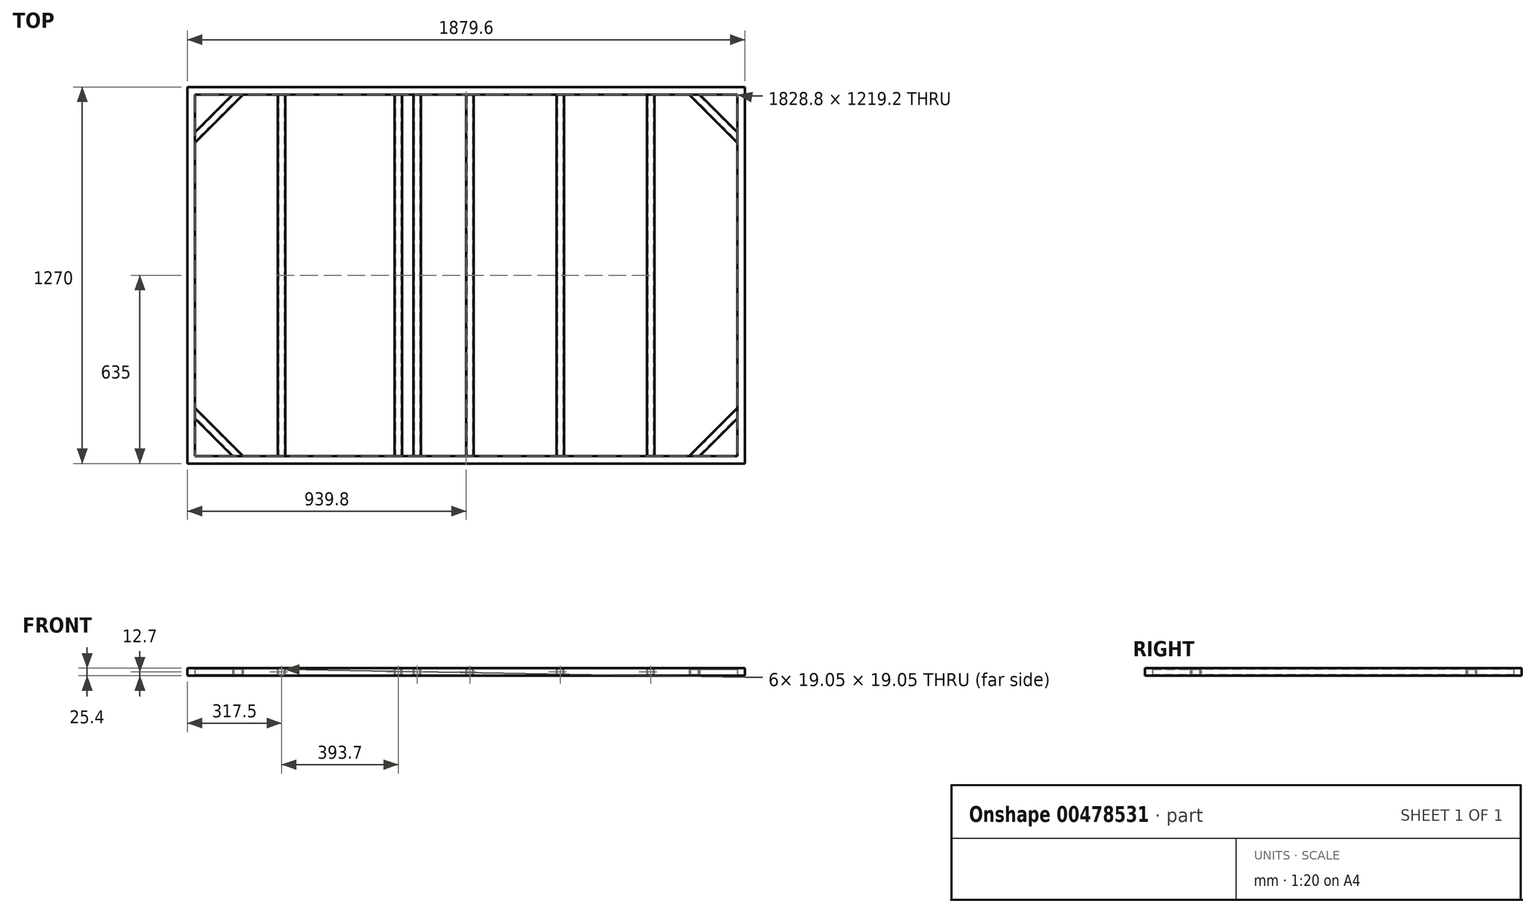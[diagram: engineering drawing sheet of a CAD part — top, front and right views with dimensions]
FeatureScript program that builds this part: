
annotation { "Feature Type Name" : "Feature", "Feature Type Description" : "" }
export const myFeature = defineFeature(function(context is Context, id is Id, definition is map)
    precondition{}
    {
        {
            var Q0;
            Q0=qCreatedBy(makeId("Top.planeOp"),FACE);
            var sketch = newSketch(context, id + "F0", { "sketchPlane" : qUnion([Q0])});
            skLineSegment(sketch, "E0.bottom", {"start": v(0, 0) * mm, "end": v(-1828.8, 0) * mm});
            skLineSegment(sketch, "E0.top", {"start": v(0, 1219.2) * mm, "end": v(-1828.8, 1219.2) * mm});
            skLineSegment(sketch, "E0.left", {"start": v(0, 0) * mm, "end": v(0, 1219.2) * mm});
            skLineSegment(sketch, "E0.right", {"start": v(-1828.8, 0) * mm, "end": v(-1828.8, 1219.2) * mm});
            skLineSegment(sketch, "E1.0", {"start": v(25.4, 1244.6) * mm, "end": v(-1854.2, 1244.6) * mm});
            skLineSegment(sketch, "E1.1", {"start": v(25.4, -25.4) * mm, "end": v(25.4, 1244.6) * mm});
            skLineSegment(sketch, "E1.2", {"start": v(25.4, -25.4) * mm, "end": v(-1854.2, -25.4) * mm});
            skLineSegment(sketch, "E1.3", {"start": v(-1854.2, -25.4) * mm, "end": v(-1854.2, 1244.6) * mm});
            skSolve(sketch);
        }
        {
            var Q0;
            Q0=makeQuery(id+"F0.imprint","IMPRINT",FACE,{"disambiguationData":[TD([[makeQuery(id+"F0.imprint","IMPRINT",EDGE,{"derivedFrom":sQuery(id+"F0.wireOp",EDGE,"E0.bottom")}),1.0]])]});
            extrude(context, id + "F1", {"entities" : qUnion([Q0]), "depth" : 25.4 * mm});
        }
        {
            var Q0;
            Q0=makeQuery(id+"F1.opExtrude","CAP_FACE",FACE,{"disambiguationData":[OSD([sQuery(id+"F0.wireOp",EDGE,"E0.bottom"),sQuery(id+"F0.wireOp",EDGE,"E0.top"),sQuery(id+"F0.wireOp",EDGE,"E0.left"),sQuery(id+"F0.wireOp",EDGE,"E0.right"),sQuery(id+"F0.wireOp",EDGE,"E1.0"),sQuery(id+"F0.wireOp",EDGE,"E1.1"),sQuery(id+"F0.wireOp",EDGE,"E1.2"),sQuery(id+"F0.wireOp",EDGE,"E1.3")])],"isStart":false});
            var sketch = newSketch(context, id + "F2", { "sketchPlane" : qUnion([Q0])});
            skLineSegment(sketch, "E2.bottom", {"start": v(-1549.4, 1219.2) * mm, "end": v(-1524, 1219.2) * mm});
            skLineSegment(sketch, "E2.top", {"start": v(-1549.4, 0) * mm, "end": v(-1524, 0) * mm});
            skLineSegment(sketch, "E2.left", {"start": v(-1549.4, 1219.2) * mm, "end": v(-1549.4, 0) * mm});
            skLineSegment(sketch, "E2.right", {"start": v(-1524, 1219.2) * mm, "end": v(-1524, 0) * mm});
            skLineSegment(sketch, "E3.bottom", {"start": v(-1092.2, 1219.2) * mm, "end": v(-1066.8, 1219.2) * mm});
            skLineSegment(sketch, "E3.top", {"start": v(-1092.2, 0) * mm, "end": v(-1066.8, 0) * mm});
            skLineSegment(sketch, "E3.left", {"start": v(-1092.2, 1219.2) * mm, "end": v(-1092.2, 0) * mm});
            skLineSegment(sketch, "E3.right", {"start": v(-1066.8, 1219.2) * mm, "end": v(-1066.8, 0) * mm});
            skLineSegment(sketch, "E4.bottom", {"start": v(-1155.7, 1219.2) * mm, "end": v(-1130.3, 1219.2) * mm});
            skLineSegment(sketch, "E4.top", {"start": v(-1155.7, 0) * mm, "end": v(-1130.3, 0) * mm});
            skLineSegment(sketch, "E4.left", {"start": v(-1130.3, 1219.2) * mm, "end": v(-1130.3, 0) * mm});
            skLineSegment(sketch, "E4.right", {"start": v(-1155.7, 1219.2) * mm, "end": v(-1155.7, 0) * mm});
            skLineSegment(sketch, "E5.bottom", {"start": v(-914.4, 1219.2) * mm, "end": v(-889, 1219.2) * mm});
            skLineSegment(sketch, "E5.top", {"start": v(-914.4, 0) * mm, "end": v(-889, 0) * mm});
            skLineSegment(sketch, "E5.left", {"start": v(-914.4, 1219.2) * mm, "end": v(-914.4, 0) * mm});
            skLineSegment(sketch, "E5.right", {"start": v(-889, 1219.2) * mm, "end": v(-889, 0) * mm});
            skLineSegment(sketch, "E6.bottom", {"start": v(-609.6, 1219.2) * mm, "end": v(-584.2, 1219.2) * mm});
            skLineSegment(sketch, "E6.top", {"start": v(-609.6, 0) * mm, "end": v(-584.2, 0) * mm});
            skLineSegment(sketch, "E6.left", {"start": v(-609.6, 1219.2) * mm, "end": v(-609.6, 0) * mm});
            skLineSegment(sketch, "E6.right", {"start": v(-584.2, 1219.2) * mm, "end": v(-584.2, 0) * mm});
            skLineSegment(sketch, "E7.bottom", {"start": v(-304.8, 1219.2) * mm, "end": v(-279.4, 1219.2) * mm});
            skLineSegment(sketch, "E7.top", {"start": v(-304.8, 0) * mm, "end": v(-279.4, 0) * mm});
            skLineSegment(sketch, "E7.left", {"start": v(-304.8, 1219.2) * mm, "end": v(-304.8, 0) * mm});
            skLineSegment(sketch, "E7.right", {"start": v(-279.4, 1219.2) * mm, "end": v(-279.4, 0) * mm});
            skSolve(sketch);
        }
        {
            var Q0;
            Q0=makeQuery(id+"F2.imprint","IMPRINT",FACE,{"disambiguationData":[TD([[makeQuery(id+"F2.imprint","IMPRINT",EDGE,{"derivedFrom":sQuery(id+"F2.wireOp",EDGE,"E2.bottom")}),1.0]])]});
            var Q1;
            Q1=makeQuery(id+"F2.imprint","IMPRINT",FACE,{"disambiguationData":[TD([[makeQuery(id+"F2.imprint","IMPRINT",EDGE,{"derivedFrom":sQuery(id+"F2.wireOp",EDGE,"E4.bottom")}),1.0]])]});
            var Q2;
            Q2=makeQuery(id+"F2.imprint","IMPRINT",FACE,{"disambiguationData":[TD([[makeQuery(id+"F2.imprint","IMPRINT",EDGE,{"derivedFrom":sQuery(id+"F2.wireOp",EDGE,"E3.bottom")}),1.0]])]});
            var Q3;
            Q3=makeQuery(id+"F2.imprint","IMPRINT",FACE,{"disambiguationData":[TD([[makeQuery(id+"F2.imprint","IMPRINT",EDGE,{"derivedFrom":sQuery(id+"F2.wireOp",EDGE,"E5.bottom")}),1.0]])]});
            var Q4;
            Q4=makeQuery(id+"F2.imprint","IMPRINT",FACE,{"disambiguationData":[TD([[makeQuery(id+"F2.imprint","IMPRINT",EDGE,{"derivedFrom":sQuery(id+"F2.wireOp",EDGE,"E6.bottom")}),1.0]])]});
            var Q5;
            Q5=makeQuery(id+"F2.imprint","IMPRINT",FACE,{"disambiguationData":[TD([[makeQuery(id+"F2.imprint","IMPRINT",EDGE,{"derivedFrom":sQuery(id+"F2.wireOp",EDGE,"E7.bottom")}),1.0]])]});
            extrude(context, id + "F3", {"entities" : qUnion([Q0, Q1, Q2, Q3, Q4, Q5]), "oppositeDirection" : true, "depth" : 25.4 * mm});
        }
        {
            var Q0;
            Q0=makeQuery(id+"F1.opExtrude","CAP_FACE",FACE,{"disambiguationData":[OSD([sQuery(id+"F0.wireOp",EDGE,"E0.bottom"),sQuery(id+"F0.wireOp",EDGE,"E0.top"),sQuery(id+"F0.wireOp",EDGE,"E0.left"),sQuery(id+"F0.wireOp",EDGE,"E0.right"),sQuery(id+"F0.wireOp",EDGE,"E1.0"),sQuery(id+"F0.wireOp",EDGE,"E1.1"),sQuery(id+"F0.wireOp",EDGE,"E1.2"),sQuery(id+"F0.wireOp",EDGE,"E1.3")])],"isStart":true});
            var sketch = newSketch(context, id + "F4", { "sketchPlane" : qUnion([Q0])});
            skLineSegment(sketch, "E8", {"start": v(-1701.8, 0) * mm, "end": v(-1828.8, -127) * mm});
            skLineSegment(sketch, "E9", {"start": v(-1665.88, 0) * mm, "end": v(-1828.8, -162.92) * mm});
            skLineSegment(sketch, "E10", {"start": v(-1828.8, -609.6) * mm, "end": v(-1335.47, -609.6) * mm, "construction": true});
            skLineSegment(sketch, "E11", {"start": v(-914.4, 25.4) * mm, "end": v(-914.4, -265.03) * mm, "construction": true});
            skPoint(sketch, "E11.endSnap0", {"position": v(-914.4, 0) * mm});
            skLineSegment(sketch, "E12.MirrorCS", {"start": v(-1701.8, -1219.2) * mm, "end": v(-1828.8, -1092.2) * mm});
            skLineSegment(sketch, "E13.MirrorCS", {"start": v(-1665.88, -1219.2) * mm, "end": v(-1828.8, -1056.28) * mm});
            skLineSegment(sketch, "E14.MirrorCS", {"start": v(-162.92, -1219.2) * mm, "end": v(0, -1056.28) * mm});
            skLineSegment(sketch, "E15.MirrorCS", {"start": v(-127, -1219.2) * mm, "end": v(0, -1092.2) * mm});
            skLineSegment(sketch, "E16.MirrorCS", {"start": v(-127, 0) * mm, "end": v(0, -127) * mm});
            skLineSegment(sketch, "E17.MirrorCS", {"start": v(-162.92, 0) * mm, "end": v(0, -162.92) * mm});
            skSolve(sketch);
        }
        {
            var Q0;
            {var subQ0=sQuery(id+"F4.wireOp",EDGE,"E8");Q0=makeQuery(id+"F4.imprint","IMPRINT",FACE,{"disambiguationData":[TD([[makeQuery(id+"F4.imprint","IMPRINT",EDGE,{"derivedFrom":subQ0}),1.0]])]});}
            var Q1;
            {var subQ0=sQuery(id+"F4.wireOp",EDGE,"E13.MirrorCS");Q1=makeQuery(id+"F4.imprint","IMPRINT",FACE,{"disambiguationData":[TD([[makeQuery(id+"F4.imprint","IMPRINT",EDGE,{"derivedFrom":subQ0}),1.0]])]});}
            var Q2;
            {var subQ0=sQuery(id+"F4.wireOp",EDGE,"E14.MirrorCS");Q2=makeQuery(id+"F4.imprint","IMPRINT",FACE,{"disambiguationData":[TD([[makeQuery(id+"F4.imprint","IMPRINT",EDGE,{"derivedFrom":subQ0}),-1.0]])]});}
            var Q3;
            {var subQ0=sQuery(id+"F4.wireOp",EDGE,"E16.MirrorCS");Q3=makeQuery(id+"F4.imprint","IMPRINT",FACE,{"disambiguationData":[TD([[makeQuery(id+"F4.imprint","IMPRINT",EDGE,{"derivedFrom":subQ0}),-1.0]])]});}
            extrude(context, id + "F5", {"entities" : qUnion([Q0, Q1, Q2, Q3]), "oppositeDirection" : true, "depth" : 25.4 * mm});
        }
        {
            var Q0;
            {var subQ0=sQuery(id+"F0.wireOp",EDGE,"E0.right");var subQ1=makeQuery(id+"F1.opExtrude","CAP_EDGE",EDGE,{"disambiguationData":[OSD([subQ0])],"isStart":true});Q0=makeQuery(id+"F5.opExtrude","SWEPT_FACE",FACE,{"disambiguationData":[OSD([subQ0]),TDD([makeQuery(id+"F4.imprint","IMPRINT",EDGE,{"disambiguationData":[TD([[makeQuery(id+"F4.imprint","INTERSECT",VERTEX,{"derivedFrom":[subQ1,sQuery(id+"F4.wireOp",EDGE,"E13.MirrorCS")]}),-1.0]])],"derivedFrom":subQ1})])]});}
            var Q1;
            {var subQ0=sQuery(id+"F0.wireOp",EDGE,"E0.top");var subQ1=makeQuery(id+"F1.opExtrude","CAP_EDGE",EDGE,{"disambiguationData":[OSD([subQ0])],"isStart":true});Q1=makeQuery(id+"F5.opExtrude","SWEPT_FACE",FACE,{"disambiguationData":[OSD([subQ0]),TDD([makeQuery(id+"F4.imprint","IMPRINT",EDGE,{"disambiguationData":[TD([[makeQuery(id+"F4.imprint","INTERSECT",VERTEX,{"derivedFrom":[subQ1,sQuery(id+"F4.wireOp",EDGE,"E13.MirrorCS")]}),-1.0]])],"derivedFrom":subQ1})])]});}
            shell(context, id + "F6", {"entities" : qUnion([Q0, Q1]), "thickness" : 3.17 * mm});
        }
        {
            var Q0;
            {var subQ0=sQuery(id+"F0.wireOp",EDGE,"E0.right");var subQ1=makeQuery(id+"F1.opExtrude","CAP_EDGE",EDGE,{"disambiguationData":[OSD([subQ0])],"isStart":true});Q0=makeQuery(id+"F5.opExtrude","SWEPT_FACE",FACE,{"disambiguationData":[OSD([subQ0]),TDD([makeQuery(id+"F4.imprint","IMPRINT",EDGE,{"disambiguationData":[TD([[makeQuery(id+"F4.imprint","INTERSECT",VERTEX,{"derivedFrom":[subQ1,sQuery(id+"F4.wireOp",EDGE,"E8")]}),-1.0]])],"derivedFrom":subQ1})])]});}
            var Q1;
            {var subQ0=sQuery(id+"F0.wireOp",EDGE,"E0.bottom");var subQ1=makeQuery(id+"F1.opExtrude","CAP_EDGE",EDGE,{"disambiguationData":[OSD([subQ0])],"isStart":true});Q1=makeQuery(id+"F5.opExtrude","SWEPT_FACE",FACE,{"disambiguationData":[OSD([subQ0]),TDD([makeQuery(id+"F4.imprint","IMPRINT",EDGE,{"disambiguationData":[TD([[makeQuery(id+"F4.imprint","INTERSECT",VERTEX,{"derivedFrom":[subQ1,sQuery(id+"F4.wireOp",EDGE,"E8")]}),1.0]])],"derivedFrom":subQ1})])]});}
            shell(context, id + "F7", {"entities" : qUnion([Q0, Q1]), "thickness" : 3.17 * mm});
        }
        {
            var Q0;
            {var subQ0=sQuery(id+"F0.wireOp",EDGE,"E0.left");var subQ1=makeQuery(id+"F1.opExtrude","CAP_EDGE",EDGE,{"disambiguationData":[OSD([subQ0])],"isStart":true});Q0=makeQuery(id+"F5.opExtrude","SWEPT_FACE",FACE,{"disambiguationData":[OSD([subQ0]),TDD([makeQuery(id+"F4.imprint","IMPRINT",EDGE,{"disambiguationData":[TD([[makeQuery(id+"F4.imprint","INTERSECT",VERTEX,{"derivedFrom":[subQ1,sQuery(id+"F4.wireOp",EDGE,"E16.MirrorCS")]}),-1.0]])],"derivedFrom":subQ1})])]});}
            var Q1;
            {var subQ0=sQuery(id+"F0.wireOp",EDGE,"E0.bottom");var subQ1=makeQuery(id+"F1.opExtrude","CAP_EDGE",EDGE,{"disambiguationData":[OSD([subQ0])],"isStart":true});Q1=makeQuery(id+"F5.opExtrude","SWEPT_FACE",FACE,{"disambiguationData":[OSD([subQ0]),TDD([makeQuery(id+"F4.imprint","IMPRINT",EDGE,{"disambiguationData":[TD([[makeQuery(id+"F4.imprint","INTERSECT",VERTEX,{"derivedFrom":[subQ1,sQuery(id+"F4.wireOp",EDGE,"E16.MirrorCS")]}),-1.0]])],"derivedFrom":subQ1})])]});}
            shell(context, id + "F8", {"entities" : qUnion([Q0, Q1]), "thickness" : 3.17 * mm});
        }
        {
            var Q0;
            {var subQ0=sQuery(id+"F0.wireOp",EDGE,"E0.left");var subQ1=makeQuery(id+"F1.opExtrude","CAP_EDGE",EDGE,{"disambiguationData":[OSD([subQ0])],"isStart":true});Q0=makeQuery(id+"F5.opExtrude","SWEPT_FACE",FACE,{"disambiguationData":[OSD([subQ0]),TDD([makeQuery(id+"F4.imprint","IMPRINT",EDGE,{"disambiguationData":[TD([[makeQuery(id+"F4.imprint","INTERSECT",VERTEX,{"derivedFrom":[subQ1,sQuery(id+"F4.wireOp",EDGE,"E14.MirrorCS")]}),-1.0]])],"derivedFrom":subQ1})])]});}
            var Q1;
            {var subQ0=sQuery(id+"F0.wireOp",EDGE,"E0.top");var subQ1=makeQuery(id+"F1.opExtrude","CAP_EDGE",EDGE,{"disambiguationData":[OSD([subQ0])],"isStart":true});Q1=makeQuery(id+"F5.opExtrude","SWEPT_FACE",FACE,{"disambiguationData":[OSD([subQ0]),TDD([makeQuery(id+"F4.imprint","IMPRINT",EDGE,{"disambiguationData":[TD([[makeQuery(id+"F4.imprint","INTERSECT",VERTEX,{"derivedFrom":[subQ1,sQuery(id+"F4.wireOp",EDGE,"E14.MirrorCS")]}),1.0]])],"derivedFrom":subQ1})])]});}
            shell(context, id + "F9", {"entities" : qUnion([Q0, Q1]), "thickness" : 3.17 * mm});
        }
        {
            var Q0;
            Q0=makeQuery(id+"F3.opExtrude","SWEPT_FACE",FACE,{"disambiguationData":[OSD([sQuery(id+"F2.wireOp",EDGE,"E7.bottom")])]});
            var Q1;
            Q1=makeQuery(id+"F3.opExtrude","SWEPT_FACE",FACE,{"disambiguationData":[OSD([sQuery(id+"F2.wireOp",EDGE,"E7.top")])]});
            var Q2;
            Q2=makeQuery(id+"F3.opExtrude","SWEPT_FACE",FACE,{"disambiguationData":[OSD([sQuery(id+"F2.wireOp",EDGE,"E6.top")])]});
            var Q3;
            Q3=makeQuery(id+"F3.opExtrude","SWEPT_FACE",FACE,{"disambiguationData":[OSD([sQuery(id+"F2.wireOp",EDGE,"E6.bottom")])]});
            var Q4;
            Q4=makeQuery(id+"F3.opExtrude","SWEPT_FACE",FACE,{"disambiguationData":[OSD([sQuery(id+"F2.wireOp",EDGE,"E5.bottom")])]});
            var Q5;
            Q5=makeQuery(id+"F3.opExtrude","SWEPT_FACE",FACE,{"disambiguationData":[OSD([sQuery(id+"F2.wireOp",EDGE,"E5.top")])]});
            var Q6;
            Q6=makeQuery(id+"F3.opExtrude","SWEPT_FACE",FACE,{"disambiguationData":[OSD([sQuery(id+"F2.wireOp",EDGE,"E3.top")])]});
            var Q7;
            Q7=makeQuery(id+"F3.opExtrude","SWEPT_FACE",FACE,{"disambiguationData":[OSD([sQuery(id+"F2.wireOp",EDGE,"E4.top")])]});
            var Q8;
            Q8=makeQuery(id+"F3.opExtrude","SWEPT_FACE",FACE,{"disambiguationData":[OSD([sQuery(id+"F2.wireOp",EDGE,"E2.top")])]});
            var Q9;
            Q9=makeQuery(id+"F3.opExtrude","SWEPT_FACE",FACE,{"disambiguationData":[OSD([sQuery(id+"F2.wireOp",EDGE,"E3.bottom")])]});
            var Q10;
            Q10=makeQuery(id+"F3.opExtrude","SWEPT_FACE",FACE,{"disambiguationData":[OSD([sQuery(id+"F2.wireOp",EDGE,"E4.bottom")])]});
            var Q11;
            Q11=makeQuery(id+"F3.opExtrude","SWEPT_FACE",FACE,{"disambiguationData":[OSD([sQuery(id+"F2.wireOp",EDGE,"E2.bottom")])]});
            shell(context, id + "F10", {"entities" : qUnion([Q0, Q1, Q2, Q3, Q4, Q5, Q6, Q7, Q8, Q9, Q10, Q11]), "thickness" : 3.17 * mm});
        }
    });
